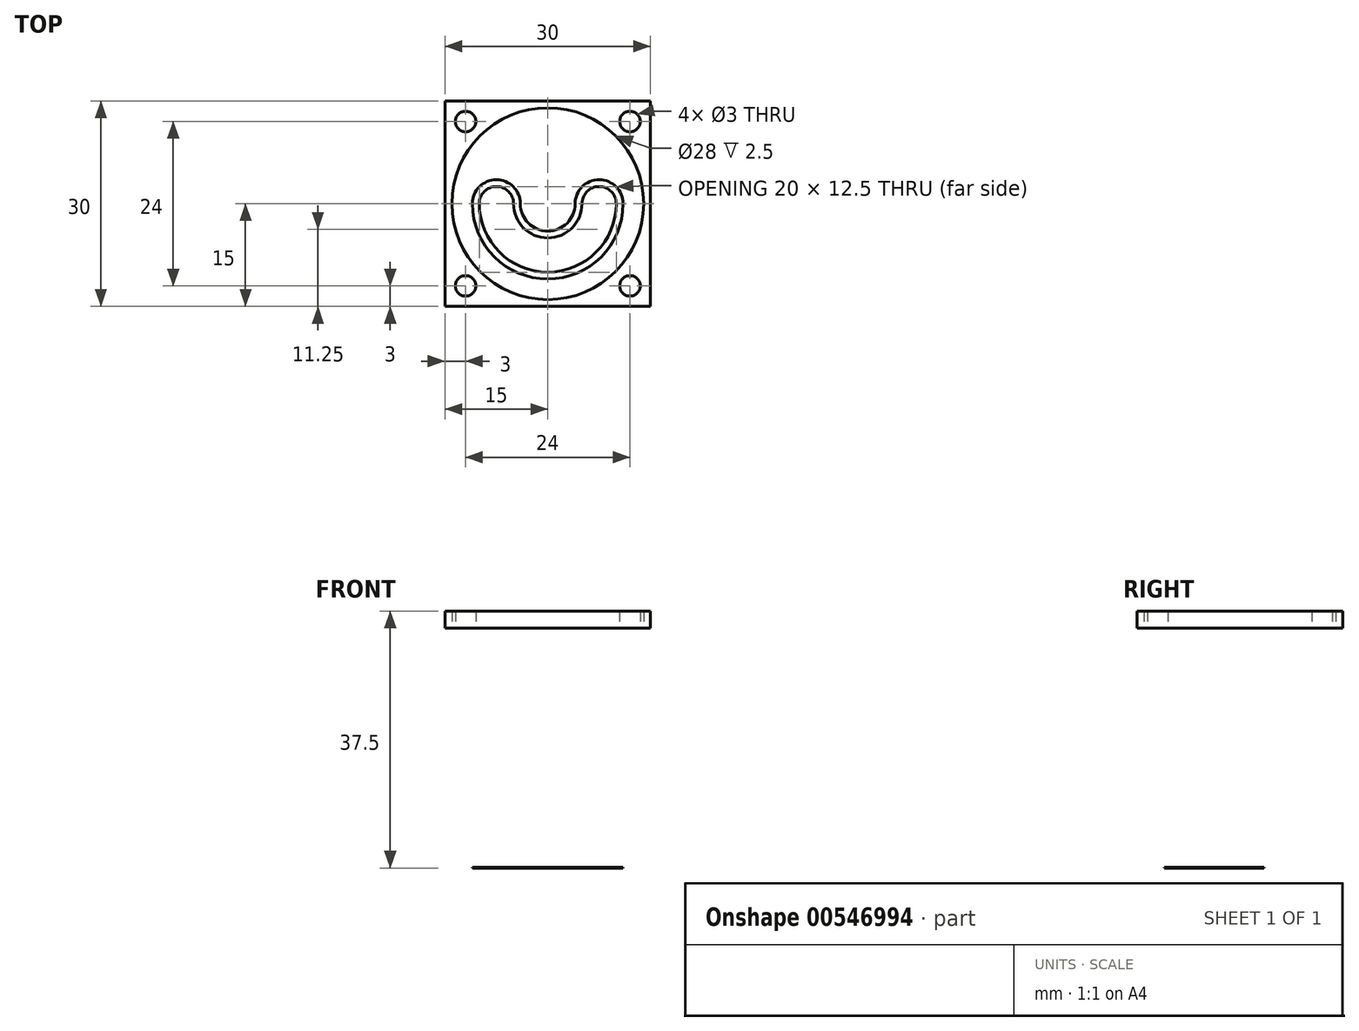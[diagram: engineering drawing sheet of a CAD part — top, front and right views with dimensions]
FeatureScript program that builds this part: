
annotation { "Feature Type Name" : "Feature", "Feature Type Description" : "" }
export const myFeature = defineFeature(function(context is Context, id is Id, definition is map)
    precondition{}
    {
        {
            var Q0;
            Q0=qCreatedBy(makeId("Top.planeOp"),FACE);
            var sketch = newSketch(context, id + "F0", { "sketchPlane" : qUnion([Q0])});
            skLineSegment(sketch, "E0.bottom", {"start": v(-15, 15) * mm, "end": v(15, 15) * mm});
            skLineSegment(sketch, "E0.top", {"start": v(-15, -15) * mm, "end": v(15, -15) * mm});
            skLineSegment(sketch, "E0.left", {"start": v(-15, 15) * mm, "end": v(-15, -15) * mm});
            skLineSegment(sketch, "E0.right", {"start": v(15, 15) * mm, "end": v(15, -15) * mm});
            skPoint(sketch, "E0.middle", {"position": v(0, 0) * mm});
            skCircle(sketch, "E1", {"center": v(-12, 12) * mm, "radius": 1.5 * mm});
            skCircle(sketch, "E2", {"center": v(-12, -12) * mm, "radius": 1.5 * mm});
            skCircle(sketch, "E3", {"center": v(12, -12) * mm, "radius": 1.5 * mm});
            skCircle(sketch, "E4", {"center": v(12, 12) * mm, "radius": 1.5 * mm});
            skCircle(sketch, "E5", {"center": v(0, 0) * mm, "radius": 14 * mm});
            skSolve(sketch);
        }
        {
            var Q0;
            Q0=makeQuery(id+"F0.imprint","IMPRINT",FACE,{"disambiguationData":[TD([[makeQuery(id+"F0.imprint","IMPRINT",EDGE,{"derivedFrom":sQuery(id+"F0.wireOp",EDGE,"E0.bottom")}),-1.0]])]});
            extrude(context, id + "F1", {"entities" : qUnion([Q0]), "depth" : 2.5 * mm, "offsetDistance" : 25 * mm});
        }
        {
            var Q0;
            Q0=qCreatedBy(makeId("Top.planeOp"),FACE);
            cPlane(context, id + "F2", {"entities" : qUnion([Q0]), "cplaneType" : CPlaneType.OFFSET, "offset" : 35 * mm, "oppositeDirection" : true, "width" : 150 * mm, "height" : 150 * mm});
        }
        {
            var Q0;
            Q0=qCreatedBy(id+"F2.planeOp",FACE);
            var sketch = newSketch(context, id + "F3", { "sketchPlane" : qUnion([Q0])});
            skArc(sketch, "E6", {"start": v(-10, 0) * mm, "mid": v(0, -10) * mm, "end": v(10, 0) * mm});
            skArc(sketch, "E7.0", {"start": v(-5, 0) * mm, "mid": v(0, -5) * mm, "end": v(5, 0) * mm});
            skArc(sketch, "E8", {"start": v(-5, 0) * mm, "mid": v(-7.5, 2.5) * mm, "end": v(-10, 0) * mm});
            skArc(sketch, "E9.MirrorC", {"start": v(5, 0) * mm, "mid": v(7.5, 2.5) * mm, "end": v(10, 0) * mm});
            skArc(sketch, "E10.0", {"start": v(-11, 0) * mm, "mid": v(0, -11) * mm, "end": v(11, 0) * mm});
            skArc(sketch, "E10.1", {"start": v(-4, 0) * mm, "mid": v(-7.5, 3.5) * mm, "end": v(-11, 0) * mm});
            skArc(sketch, "E10.2", {"start": v(-4, 0) * mm, "mid": v(0, -4) * mm, "end": v(4, 0) * mm});
            skArc(sketch, "E10.3", {"start": v(4, 0) * mm, "mid": v(7.5, 3.5) * mm, "end": v(11, 0) * mm});
            skSolve(sketch);
        }
        {
            var Q0;
            Q0 = qSketchRegion(id + "F3", true);
            extrude(context, id + "F4", {"entities" : qUnion([Q0]), "depth" : .1 * mm, "offsetDistance" : 25 * mm});
        }
    });
